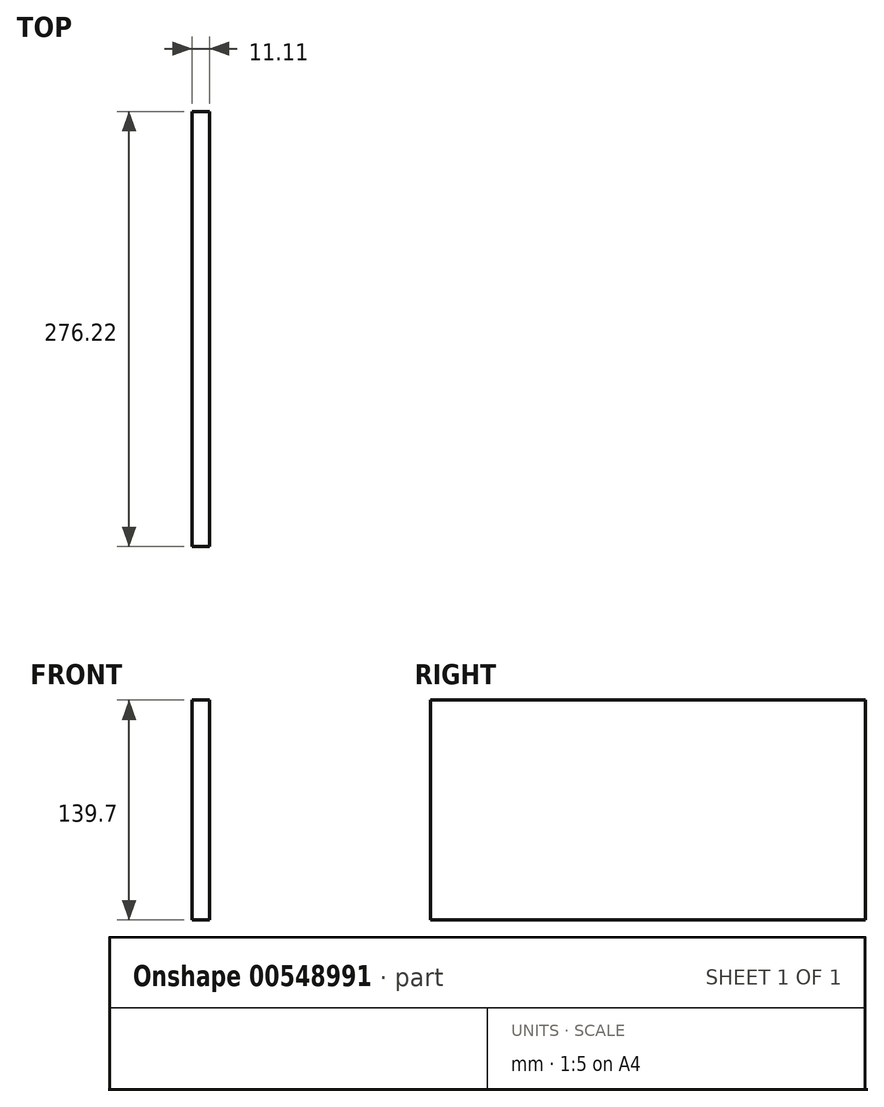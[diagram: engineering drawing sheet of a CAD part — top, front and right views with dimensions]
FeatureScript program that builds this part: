
annotation { "Feature Type Name" : "Feature", "Feature Type Description" : "" }
export const myFeature = defineFeature(function(context is Context, id is Id, definition is map)
    precondition{}
    {
        {
            var Q0;
            Q0=qCreatedBy(makeId("Right.planeOp"),FACE);
            var sketch = newSketch(context, id + "F0", { "sketchPlane" : qUnion([Q0])});
            skLineSegment(sketch, "E0.bottom", {"start": v(138.11, 69.85) * mm, "end": v(-138.11, 69.85) * mm});
            skLineSegment(sketch, "E0.top", {"start": v(138.11, -69.85) * mm, "end": v(-138.11, -69.85) * mm});
            skLineSegment(sketch, "E0.left", {"start": v(138.11, 69.85) * mm, "end": v(138.11, -69.85) * mm});
            skLineSegment(sketch, "E0.right", {"start": v(-138.11, 69.85) * mm, "end": v(-138.11, -69.85) * mm});
            skPoint(sketch, "E0.middle", {"position": v(0, 0) * mm});
            skSolve(sketch);
        }
        {
            var Q0;
            Q0 = qSketchRegion(id + "F0", true);
            extrude(context, id + "F1", {"entities" : qUnion([Q0]), "depth" : 11.1 * mm, "offsetDistance" : 25.4 * mm});
        }
    });
